# Revit family: Semi Recessed Lavatory_TOTO_LW533
name_source: partatom
category: 衛生器具
revit_build: Autodesk Revit 2018 (Build: 20181011_1500(x64)
units: mm (PartAtom-declared; Revit-internal decimal feet)

## family parameters
OmniClass タイトル = Sanitary, Laundry, and Cleaning Equipment
OmniClass 番号 = 23.45.00.00
パーツ タイプ = 標準
ロード時にボイドで切り取り = いいえ
丸型コネクタ寸法 = 直径を使用
作業面ベース = いいえ
共有 = いいえ
常に垂直 = はい
部屋計算ポイント = いいえ

## types (1)
- Semi Recessed Lavatory_TOTO_LW533
    Finish = basin_material
    Height = 175  [stored 0.574147 ft]
    Length = 430  [stored 1.41076 ft]
    TOTO HongKong = LW533J
    TOTO HongKong URL = http://hk.toto.com
    TOTO Korea = LW533J
    TOTO Korea URL = https://kr.toto.com
    TOTO Taiwan = LW533JU
    TOTO Taiwan URL = https://www.twtoto.com.tw
    TOTO Thailand = LW533JW/F
    TOTO Thailand URL = https://th.toto.com
    TOTO Vietnam = LT533R
    TOTO Vietnam URL = https://vn.toto.com
    Width = 430  [stored 1.41076 ft]
    排気配管 = いいえ
    排水配管 = いいえ
    水配管 = いいえ
    温水配管 = いいえ
    製造元 = TOTO Ltd.
    説明 = Semi Recessed Lavatory/半嵌式脸盆

note: [stored X ft] marks values corroborated as IEEE doubles in the binary element streams (Revit-internal decimal feet)

## geometry (parser evidence)
native form markers: Sweep x2
no freeform markers — native parametric forms only
